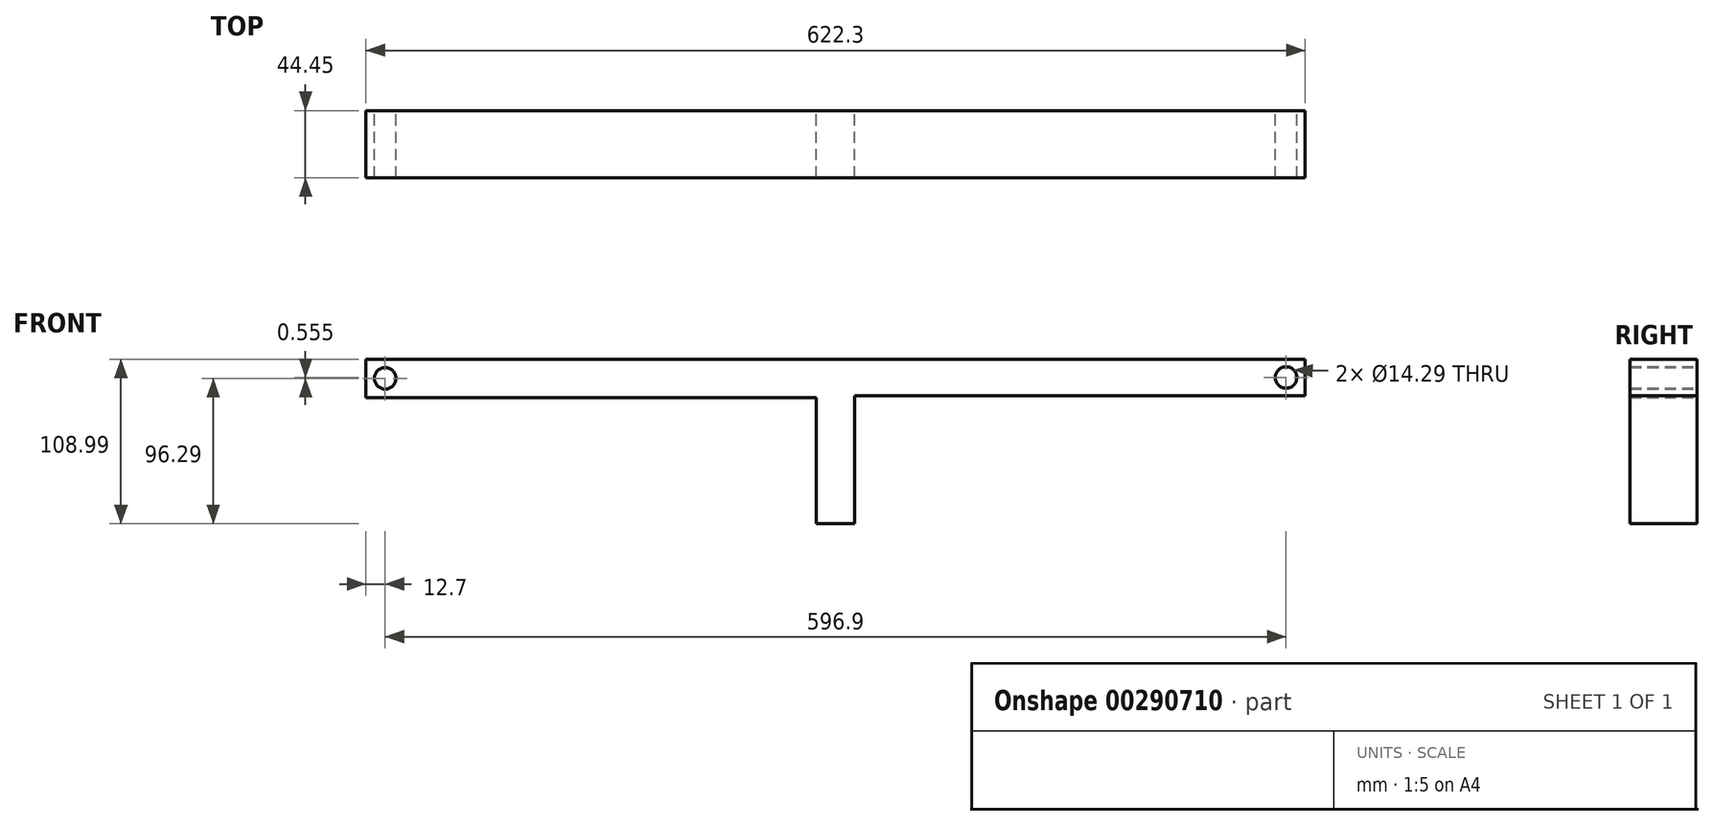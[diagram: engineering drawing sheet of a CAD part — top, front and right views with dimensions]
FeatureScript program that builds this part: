
annotation { "Feature Type Name" : "Feature", "Feature Type Description" : "" }
export const myFeature = defineFeature(function(context is Context, id is Id, definition is map)
    precondition{}
    {
        {
            var Q0;
            Q0=qCreatedBy(makeId("Front.planeOp"),FACE);
            var sketch = newSketch(context, id + "F0", { "sketchPlane" : qUnion([Q0])});
            skLineSegment(sketch, "E0", {"start": v(0, 0) * mm, "end": v(0, -25.4) * mm});
            skLineSegment(sketch, "E1", {"start": v(0, -25.4) * mm, "end": v(298.45, -25.4) * mm});
            skLineSegment(sketch, "E2", {"start": v(298.45, -25.4) * mm, "end": v(298.45, -109) * mm});
            skLineSegment(sketch, "E3", {"start": v(298.45, -109) * mm, "end": v(323.85, -109) * mm});
            skLineSegment(sketch, "E4", {"start": v(323.85, -109) * mm, "end": v(323.85, -24.3) * mm});
            skLineSegment(sketch, "E5", {"start": v(323.85, -24.3) * mm, "end": v(622.3, -24.3) * mm});
            skLineSegment(sketch, "E6", {"start": v(622.3, -24.3) * mm, "end": v(622.3, 0) * mm});
            skLineSegment(sketch, "E7", {"start": v(622.3, 0) * mm, "end": v(0, 0) * mm});
            skCircle(sketch, "E8", {"center": v(12.7, -12.7) * mm, "radius": 7.14 * mm});
            skPoint(sketch, "E8.centerSnap0", {"position": v(0, -12.7) * mm});
            skCircle(sketch, "E9", {"center": v(609.6, -12.15) * mm, "radius": 7.14 * mm});
            skPoint(sketch, "E9.centerSnap0", {"position": v(622.3, -12.15) * mm});
            skPoint(sketch, "E10", {"position": v(311.15, -109) * mm});
            skPoint(sketch, "E11", {"position": v(311.15, 0) * mm});
            skSolve(sketch);
        }
        {
            var Q0;
            Q0=makeQuery(id+"F0.imprint","IMPRINT",FACE,{"disambiguationData":[TD([[makeQuery(id+"F0.imprint","IMPRINT",EDGE,{"derivedFrom":sQuery(id+"F0.wireOp",EDGE,"E0")}),1.0]])]});
            extrude(context, id + "F1", {"entities" : qUnion([Q0]), "depth" : 44.45 * mm});
        }
    });
